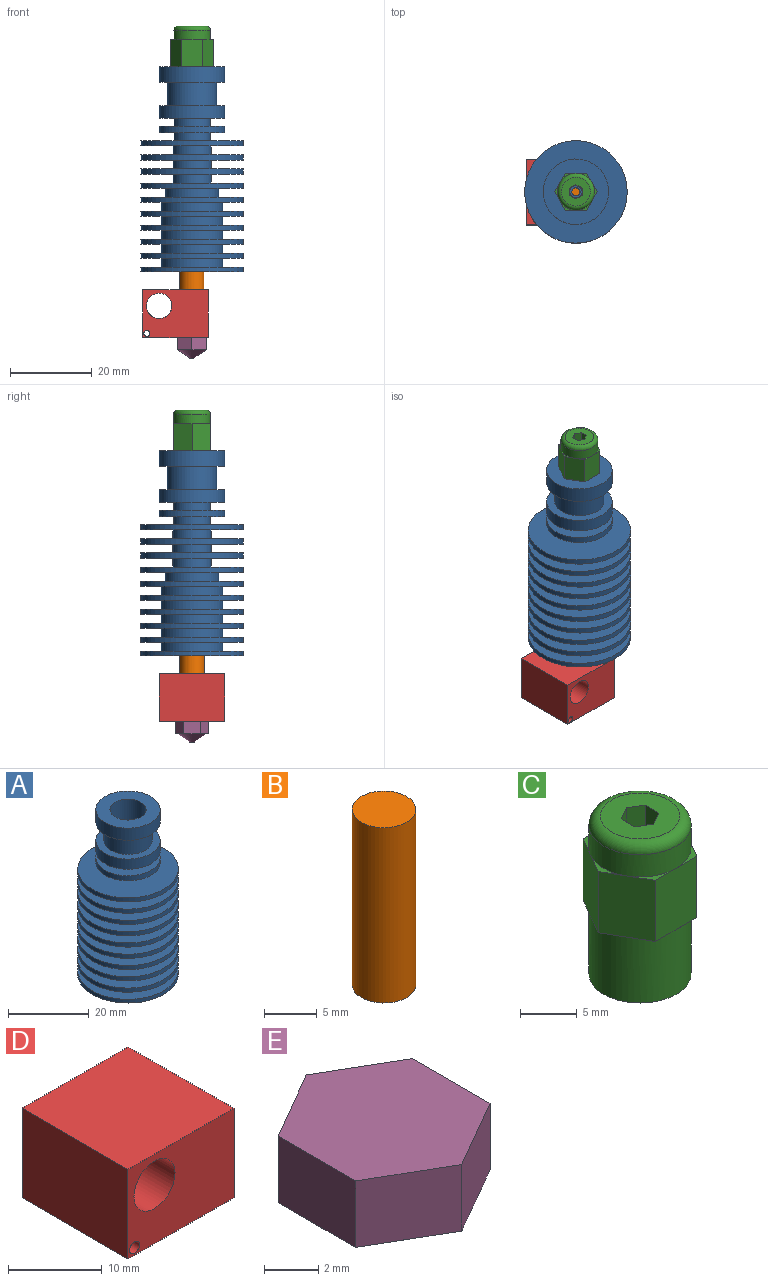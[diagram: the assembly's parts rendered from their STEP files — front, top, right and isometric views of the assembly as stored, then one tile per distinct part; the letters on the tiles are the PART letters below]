
ASSEMBLY  parts=5 mates=4
PART A: 57 faces, bbox 25x25x50 mm
  f0: cylinder r=8mm len=16mm, axis (0,0,-1), area 75.4mm2, adj f40,f43
  f1: cylinder r=12.5mm len=25mm, axis (0,0,-1), area 98.2mm2, adj f33,f37
  f2: cylinder r=12.5mm len=25mm, axis (0,0,-1), area 98.2mm2, adj f30,f34
  f3: cylinder r=12.5mm len=25mm, axis (0,0,-1), area 98.2mm2, adj f27,f31
  f4: cylinder r=12.5mm len=25mm, axis (0,0,-1), area 98.2mm2, adj f24,f28
  f5: cylinder r=12.5mm len=25mm, axis (0,0,-1), area 98.2mm2, adj f21,f25
  f6: cylinder r=12.5mm len=25mm, axis (0,0,-1), area 98.2mm2, adj f18,f22
  f7: cylinder r=12.5mm len=25mm, axis (0,0,-1), area 98.2mm2, adj f15,f19
  f8: cylinder r=12.5mm len=25mm, axis (0,0,-1), area 98.2mm2, adj f10,f16
  f9: cylinder r=7.5mm len=15mm, axis (0,0,-1), area 102.8mm2, adj f10,f11
  f10: plane 25x25mm, normal (0,0,-1), area 314.2mm2, adj f8,f9
  f11: plane 25x25mm, normal (0,0,1), area 314.2mm2, adj f9,f13
  f12: plane 25x25mm, normal (0,0,-1), area 462.6mm2, adj f13,f51
  f13: cylinder r=12.5mm len=25mm, axis (0,0,-1), area 86.4mm2, adj f11,f12
  f14: cylinder r=7.5mm len=15mm, axis (0,0,-1), area 102.8mm2, adj f15,f16
  f15: plane 25x25mm, normal (0,0,-1), area 314.2mm2, adj f7,f14
  f16: plane 25x25mm, normal (0,0,1), area 314.2mm2, adj f8,f14
  f17: cylinder r=7.5mm len=15mm, axis (0,0,-1), area 102.8mm2, adj f18,f19
  f18: plane 25x25mm, normal (0,0,-1), area 314.2mm2, adj f6,f17
  f19: plane 25x25mm, normal (0,0,1), area 314.2mm2, adj f7,f17
  f20: cylinder r=7.5mm len=15mm, axis (0,0,-1), area 102.8mm2, adj f21,f22
  f21: plane 25x25mm, normal (0,0,-1), area 314.2mm2, adj f5,f20
  f22: plane 25x25mm, normal (0,0,1), area 314.2mm2, adj f6,f20
  f23: cylinder r=7.5mm len=15mm, axis (0,0,-1), area 102.8mm2, adj f24,f25
  f24: plane 25x25mm, normal (0,0,-1), area 314.2mm2, adj f4,f23
  f25: plane 25x25mm, normal (0,0,1), area 314.2mm2, adj f5,f23
  f26: cylinder r=6.5mm len=13mm, axis (0,0,-1), area 89.1mm2, adj f27,f28
  f27: plane 25x25mm, normal (0,0,-1), area 358.1mm2, adj f3,f26
  f28: plane 25x25mm, normal (0,0,1), area 358.1mm2, adj f4,f26
  f29: cylinder r=4.68mm len=9.36mm, axis (0,0,-1), area 64.1mm2, adj f30,f31
  f30: plane 25x25mm, normal (0,0,-1), area 422.1mm2, adj f2,f29
  f31: plane 25x25mm, normal (0,0,1), area 422.1mm2, adj f3,f29
  f32: cylinder r=4.68mm len=9.36mm, axis (0,0,-1), area 64.1mm2, adj f33,f34
  f33: plane 25x25mm, normal (0,0,-1), area 422.1mm2, adj f1,f32
  f34: plane 25x25mm, normal (0,0,1), area 422.1mm2, adj f2,f32
  f35: cylinder r=4.68mm len=9.36mm, axis (0,0,-1), area 64.1mm2, adj f36,f37
  f36: plane 25x25mm, normal (0,0,-1), area 422.1mm2, adj f35,f39
  f37: plane 25x25mm, normal (0,0,1), area 422.1mm2, adj f1,f35
  f38: plane 25x25mm, normal (0,0,1), area 427.3mm2, adj f39,f41
  f39: cylinder r=12.5mm len=25mm, axis (0,0,-1), area 99.6mm2, adj f36,f38
  f40: plane 16x16mm, normal (0,0,-1), area 137.4mm2, adj f0,f41
  f41: cylinder r=4.5mm len=9mm, axis (0,0,-1), area 56.5mm2, adj f38,f40
  f42: plane 16x16mm, normal (0,0,-1), area 137.4mm2, adj f44,f50
  f43: plane 16x16mm, normal (0,0,1), area 137.4mm2, adj f0,f44
  f44: cylinder r=4.5mm len=9mm, axis (0,0,-1), area 56.5mm2, adj f42,f43
  f45: plane 16x16mm, normal (0,0,1), area 137.4mm2, adj f46,f53
  f46: cylinder r=8mm len=16mm, axis (0,0,-1), area 186mm2, adj f45,f47
  f47: plane 16x16mm, normal (0,0,-1), area 88mm2, adj f46,f48
  f48: cylinder r=6mm len=12mm, axis (0,0,1), area 214.9mm2, adj f47,f49
  f49: plane 16x16mm, normal (0,0,1), area 88mm2, adj f48,f50
  f50: cylinder r=8mm len=16mm, axis (0,0,-1), area 155.8mm2, adj f42,f49
  f51: cylinder r=3mm len=18mm, axis (0,0,-1), area 339.3mm2, adj f12,f52
  f52: plane 6x6mm, normal (0,0,-1), area 25.1mm2, adj f51,f55
  f53: cylinder r=4.5mm len=10.27mm, axis (0,0,1), area 290.3mm2, adj f45,f56
  f54: plane 3x3mm, normal (0,0,1), area 3.9mm2, adj f55,f56
  f55: cylinder r=1mm len=20mm, axis (0,0,1), area 125.7mm2, adj f52,f54
  f56: cone r=1.5mm half-angle=60deg, axis (0,0,1), area 65.3mm2, adj f53,f54
PART B: 3 faces, bbox 6x6x20.3 mm
  f0: cylinder r=3mm len=20.3mm, axis (0,0,1), area 382.6mm2, adj f1,f2
  f1: plane 6x6mm, normal (0,0,-1), area 28.3mm2, adj f0
  f2: plane 6x6mm, normal (0,0,1), area 28.3mm2, adj f0
PART C: 29 faces, bbox 10.4x9.7x17 mm
  f0: plane 7x7mm, normal (0,0,1), area 30.7mm2, adj f22,f23,f24,f25,f26,f27,f28
  f1: plane 9x9mm, normal (0,0,-1), area 55.8mm2, adj f21,f23,f24,f25,f26,f27,f28
  f2: cylinder r=4.5mm len=9mm, axis (0,0,1), area 67.9mm2, adj f9,f10,f11,f12,f13,f19,f22
  f3: plane 6.6x5.2mm, normal (0,1,0), area 34.3mm2, adj f4,f8,f12,f13,f17,f18
  f4: plane 6.6x4.5mm, normal (-0.87,0.5,0), area 34.3mm2, adj f3,f5,f11,f12,f16,f17
  f5: plane 6.6x4.5mm, normal (-0.87,-0.5,0), area 34.3mm2, adj f4,f6,f10,f11,f15,f16
  f6: plane 6.6x5.2mm, normal (0,-1,0), area 34.3mm2, adj f5,f7,f9,f10,f14,f15
  f7: plane 6.6x4.5mm, normal (0.87,-0.5,0), area 34.3mm2, adj f6,f8,f9,f14,f19,f20
  f8: plane 6.6x4.5mm, normal (0.87,0.5,0), area 34.3mm2, adj f3,f7,f13,f18,f19,f20
  f9: plane 3.9x2.25mm, normal (0,0,1), area 1.1mm2, adj f2,f6,f7
  f10: plane 3.9x2.25mm, normal (0,0,1), area 1.1mm2, adj f2,f5,f6
  f11: plane 4.5x1.3mm, normal (0,0,1), area 1.1mm2, adj f2,f4,f5
  f12: plane 3.9x2.25mm, normal (0,0,1), area 1.1mm2, adj f2,f3,f4
  f13: plane 3.9x2.25mm, normal (0,0,1), area 1.1mm2, adj f2,f3,f8
  f14: plane 3.9x2.25mm, normal (0,0,-1), area 1.1mm2, adj f6,f7,f21
  f15: plane 3.9x2.25mm, normal (0,0,-1), area 1.1mm2, adj f5,f6,f21
  f16: plane 4.5x1.3mm, normal (0,0,-1), area 1.1mm2, adj f4,f5,f21
  f17: plane 3.9x2.25mm, normal (0,0,-1), area 1.1mm2, adj f3,f4,f21
  f18: plane 3.9x2.25mm, normal (0,0,-1), area 1.1mm2, adj f3,f8,f21
  f19: plane 4.5x1.3mm, normal (0,0,1), area 1.1mm2, adj f2,f7,f8
  f20: plane 4.5x1.3mm, normal (0,0,-1), area 1.1mm2, adj f7,f8,f21
  f21: cylinder r=4.5mm len=9mm, axis (0,0,1), area 197.9mm2, adj f1,f14,f15,f16,f17,f18,f20
  f22: torus R=3.5mm, axis (0,0,1), area 40.8mm2, adj f0,f2
  f23: plane 17x1.5mm, normal (0.5,0.87,0), area 29.4mm2, adj f0,f1,f24,f28
  f24: plane 17x1.5mm, normal (-0.5,0.87,0), area 29.4mm2, adj f0,f1,f23,f25
  f25: plane 17x1.73mm, normal (-1,0,0), area 29.4mm2, adj f0,f1,f24,f26
  f26: plane 17x1.5mm, normal (-0.5,-0.87,0), area 29.4mm2, adj f0,f1,f25,f27
  f27: plane 17x1.5mm, normal (0.5,-0.87,0), area 29.4mm2, adj f0,f1,f26,f28
  f28: plane 17x1.73mm, normal (1,0,0), area 29.4mm2, adj f0,f1,f23,f27
PART D: 9 faces, bbox 16x16x11.7 mm
  f0: plane 16x11.7mm, normal (-1,0,0), area 187.2mm2, adj f1,f3,f4,f5
  f1: plane 16x11.7mm, normal (0,1,0), area 155.2mm2, adj f0,f2,f4,f5,f6,f7
  f2: plane 16x11.7mm, normal (1,0,0), area 187.2mm2, adj f1,f3,f4,f5
  f3: plane 16x11.7mm, normal (0,-1,0), area 155.2mm2, adj f0,f2,f4,f5,f6,f7
  f4: plane 16x16mm, normal (0,0,-1), area 255.2mm2, adj f0,f1,f2,f3,f8
  f5: plane 16x16mm, normal (0,0,1), area 256mm2, adj f0,f1,f2,f3
  f6: cylinder r=0.75mm len=16mm, axis (0,1,0), area 75.4mm2, adj f1,f3
  f7: cylinder r=3.1mm len=16mm, axis (0,1,0), area 310.9mm2, adj f1,f3,f8
  f8: cylinder r=0.5mm len=4.64mm, axis (0,0,-1), area 14.5mm2, adj f4,f7
PART E: 15 faces, bbox 7x8.1x5 mm
  f0: plane 3.03x1.75mm, normal (0,0,-1), area 0.7mm2, adj f5,f6,f14
  f1: plane 3.5x1.01mm, normal (0,0,-1), area 0.7mm2, adj f6,f7,f14
  f2: plane 3.03x1.75mm, normal (0,0,-1), area 0.7mm2, adj f7,f8,f14
  f3: plane 3.03x1.75mm, normal (0,0,-1), area 0.7mm2, adj f8,f9,f14
  f4: plane 3.5x1.01mm, normal (0,0,-1), area 0.7mm2, adj f9,f10,f14
  f5: plane 4.04x3mm, normal (-1,0,0), area 12.1mm2, adj f0,f6,f10,f11,f12
  f6: plane 3.5x3mm, normal (-0.5,0.87,0), area 12.1mm2, adj f0,f1,f5,f7,f12
  f7: plane 3.5x3mm, normal (0.5,0.87,0), area 12.1mm2, adj f1,f2,f6,f8,f12
  f8: plane 4.04x3mm, normal (1,0,0), area 12.1mm2, adj f2,f3,f7,f9,f12
  f9: plane 3.5x3mm, normal (0.5,-0.87,0), area 12.1mm2, adj f3,f4,f8,f10,f12
  f10: plane 3.5x3mm, normal (-0.5,-0.87,0), area 12.1mm2, adj f4,f5,f9,f11,f12
  f11: plane 3.03x1.75mm, normal (0,0,-1), area 0.7mm2, adj f5,f10,f14
  f12: plane 8.08x7mm, normal (0,0,1), area 42.4mm2, adj f5,f6,f7,f8,f9,f10
  f13: plane 1x1mm, normal (0,0,-1), area 0.8mm2, adj f14
  f14: cone r=0.5mm half-angle=56.3deg, axis (0,0,1), area 45.3mm2, adj f0,f1,f2,f3,f4,f11,f13
PLACE A t=(13923.74,3872.27,-6269.4)mm
PLACE B t=(13923.74,3872.27,-6269.4)mm
PLACE C t=(13923.74,3872.27,-6269.4)mm
PLACE D t=(13923.74,3872.27,-6269.4)mm
PLACE E t=(13923.74,3872.27,-6269.4)mm
MATE fastened D.f5 <-> B.f1  axis (0,0,1) through (13927.74,3872.27,-6273.7)mm
MATE fastened C.f2 <-> A.f53  axis (0,0,1) through (13923.74,3872.27,-6219.4)mm
MATE fastened B.f0 <-> A.f51  axis (0,0,1) through (13923.74,3872.27,-6253.4)mm
MATE fastened E.f14 <-> D.f4  axis (0,0,1) through (13923.74,3872.27,-6285.4)mm
